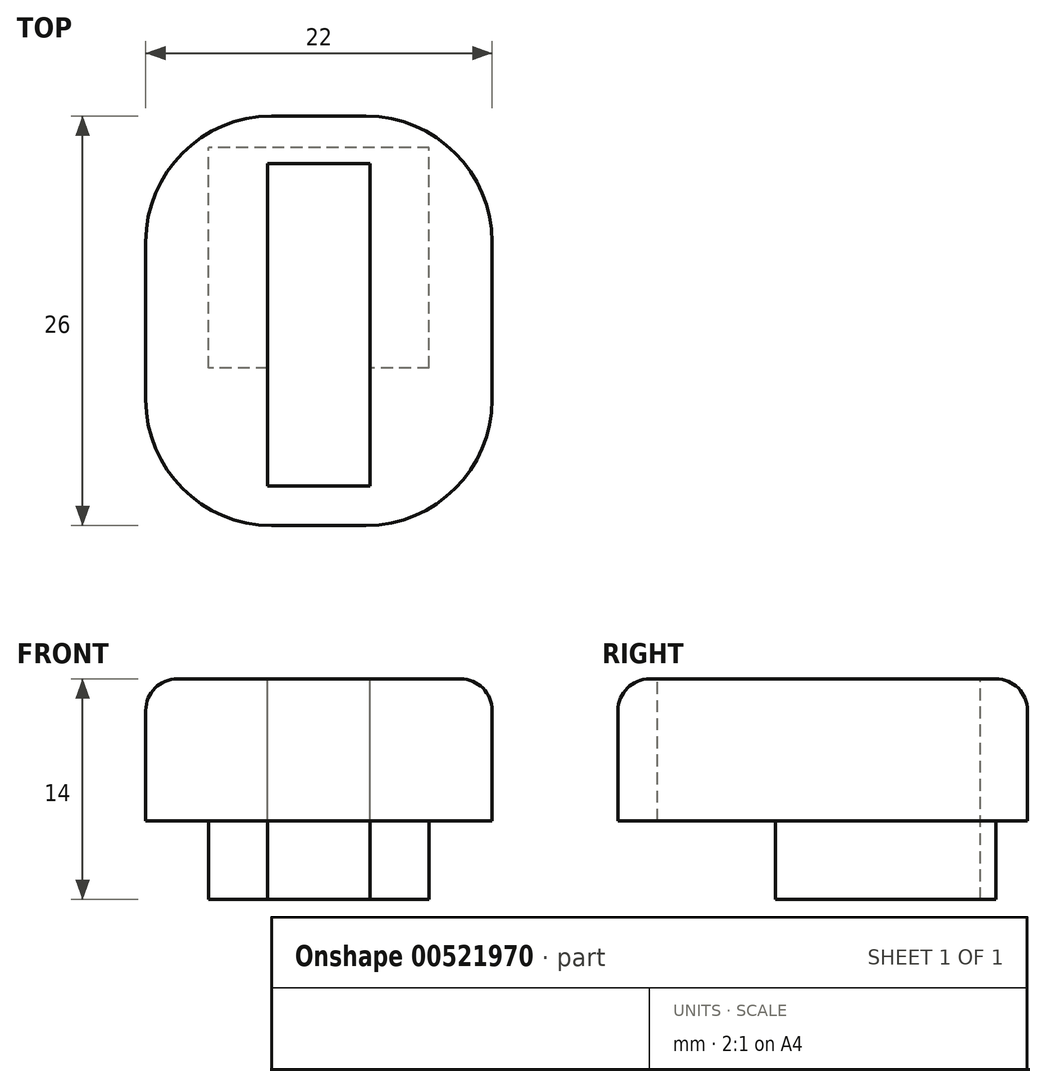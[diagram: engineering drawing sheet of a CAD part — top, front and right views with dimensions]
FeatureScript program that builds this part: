
annotation { "Feature Type Name" : "Feature", "Feature Type Description" : "" }
export const myFeature = defineFeature(function(context is Context, id is Id, definition is map)
    precondition{}
    {
        {
            var Q0;
            Q0=qCreatedBy(makeId("Top.planeOp"),FACE);
            var sketch = newSketch(context, id + "F0", { "sketchPlane" : qUnion([Q0])});
            skLineSegment(sketch, "E0.bottom", {"start": v(0, 0) * mm, "end": v(-14, 0) * mm});
            skLineSegment(sketch, "E0.top", {"start": v(0, 14) * mm, "end": v(-14, 14) * mm});
            skLineSegment(sketch, "E0.left", {"start": v(0, 0) * mm, "end": v(0, 14) * mm});
            skLineSegment(sketch, "E0.right", {"start": v(-14, 0) * mm, "end": v(-14, 14) * mm});
            skSolve(sketch);
        }
        {
            var Q0;
            Q0 = qSketchRegion(id + "F0", true);
            var Q1;
            Q1=makeQuery(id+"F0.imprint","IMPRINT",FACE,{"disambiguationData":[TD([[makeQuery(id+"F0.imprint","IMPRINT",EDGE,{"derivedFrom":sQuery(id+"F0.wireOp",EDGE,"E0.bottom")}),-1.0]])]});
            extrude(context, id + "F1", {"entities" : qUnion([Q0, Q1]), "depth" : 5 * mm, "offsetDistance" : 25 * mm});
        }
        {
            var Q0;
            Q0=makeQuery(id+"F1.opExtrude","CAP_FACE",FACE,{"disambiguationData":[OSD([sQuery(id+"F0.wireOp",EDGE,"E0.bottom"),sQuery(id+"F0.wireOp",EDGE,"E0.top"),sQuery(id+"F0.wireOp",EDGE,"E0.left"),sQuery(id+"F0.wireOp",EDGE,"E0.right")])],"isStart":false});
            var sketch = newSketch(context, id + "F2", { "sketchPlane" : qUnion([Q0])});
            skLineSegment(sketch, "E1.bottom", {"start": v(-18, 16) * mm, "end": v(4, 16) * mm});
            skLineSegment(sketch, "E1.top", {"start": v(-18, -10) * mm, "end": v(4, -10) * mm});
            skLineSegment(sketch, "E1.left", {"start": v(-18, 16) * mm, "end": v(-18, -10) * mm});
            skLineSegment(sketch, "E1.right", {"start": v(4, 16) * mm, "end": v(4, -10) * mm});
            skSolve(sketch);
        }
        {
            var Q0;
            Q0=makeQuery(id+"F2.imprint","IMPRINT",FACE,{"disambiguationData":[TD([[makeQuery(id+"F2.imprint","IMPRINT",EDGE,{"derivedFrom":sQuery(id+"F2.wireOp",EDGE,"E1.bottom")}),-1.0]])]});
            var Q1;
            Q1=makeQuery(id+"F2.imprint","IMPRINT",FACE,{"disambiguationData":[TD([[makeQuery(id+"F2.imprint","IMPRINT",EDGE,{"derivedFrom":makeQuery(id+"F1.opExtrude","CAP_EDGE",EDGE,{"disambiguationData":[OSD([sQuery(id+"F0.wireOp",EDGE,"E0.bottom")])],"isStart":false})}),-1.0]])]});
            extrude(context, id + "F3", {"entities" : qUnion([Q0, Q1]), "operationType" : NewBodyOperationType.ADD, "depth" : 9 * mm, "offsetDistance" : 25 * mm});
        }
        {
            var Q0;
            Q0=makeQuery(id+"F3.opExtrude","CAP_FACE",FACE,{"disambiguationData":[OSD([sQuery(id+"F2.wireOp",EDGE,"E1.bottom"),sQuery(id+"F2.wireOp",EDGE,"E1.top"),sQuery(id+"F2.wireOp",EDGE,"E1.left"),sQuery(id+"F2.wireOp",EDGE,"E1.right")])],"isStart":false});
            var sketch = newSketch(context, id + "F4", { "sketchPlane" : qUnion([Q0])});
            skLineSegment(sketch, "E2.bottom", {"start": v(-10.25, 13) * mm, "end": v(-3.75, 13) * mm});
            skLineSegment(sketch, "E2.top", {"start": v(-10.25, -7.5) * mm, "end": v(-3.75, -7.5) * mm});
            skLineSegment(sketch, "E2.left", {"start": v(-10.25, 13) * mm, "end": v(-10.25, -7.5) * mm});
            skLineSegment(sketch, "E2.right", {"start": v(-3.75, 13) * mm, "end": v(-3.75, -7.5) * mm});
            skLineSegment(sketch, "E3", {"start": v(-7, 13) * mm, "end": v(-7, 16) * mm, "construction": true});
            skSolve(sketch);
        }
        {
            var Q0;
            Q0=makeQuery(id+"F4.imprint","IMPRINT",FACE,{"disambiguationData":[TD([[makeQuery(id+"F4.imprint","IMPRINT",EDGE,{"derivedFrom":sQuery(id+"F4.wireOp",EDGE,"E2.bottom")}),-1.0]])]});
            var Q1;
            Q1=makeQuery(id+"F3.opExtrude","CAP_FACE",FACE,{"disambiguationData":[OSD([sQuery(id+"F2.wireOp",EDGE,"E1.bottom"),sQuery(id+"F2.wireOp",EDGE,"E1.top"),sQuery(id+"F2.wireOp",EDGE,"E1.left"),sQuery(id+"F2.wireOp",EDGE,"E1.right")])],"isStart":true});
            extrude(context, id + "F5", {"entities" : qUnion([Q0]), "operationType" : NewBodyOperationType.REMOVE, "endBound" : BoundingType.UP_TO_SURFACE, "oppositeDirection" : true, "depth" : 25 * mm, "endBoundEntityFace" : qUnion([Q1]), "offsetDistance" : 25 * mm});
        }
        {
            var Q0;
            Q0=makeQuery(id+"F5.boolean.opBoolean","COPY",FACE,{"derivedFrom":makeQuery(id+"F5.opExtrude","CAP_FACE",FACE,{"disambiguationData":[OSD([sQuery(id+"F4.wireOp",EDGE,"E2.bottom"),sQuery(id+"F4.wireOp",EDGE,"E2.top"),sQuery(id+"F4.wireOp",EDGE,"E2.left"),sQuery(id+"F4.wireOp",EDGE,"E2.right")])],"isStart":false})});
            var sketch = newSketch(context, id + "F6", { "sketchPlane" : qUnion([Q0])});
            skLineSegment(sketch, "E4.bottom", {"start": v(-3.75, 13) * mm, "end": v(-10.25, 13) * mm});
            skLineSegment(sketch, "E4.top", {"start": v(-3.75, 0) * mm, "end": v(-10.25, 0) * mm});
            skLineSegment(sketch, "E4.left", {"start": v(-3.75, 13) * mm, "end": v(-3.75, 0) * mm});
            skLineSegment(sketch, "E4.right", {"start": v(-10.25, 13) * mm, "end": v(-10.25, 0) * mm});
            skSolve(sketch);
        }
        {
            var Q0;
            Q0=makeQuery(id+"F6.imprint","IMPRINT",FACE,{"disambiguationData":[TD([[makeQuery(id+"F6.imprint","IMPRINT",EDGE,{"derivedFrom":sQuery(id+"F6.wireOp",EDGE,"E4.bottom")}),1.0]])]});
            extrude(context, id + "F7", {"entities" : qUnion([Q0]), "operationType" : NewBodyOperationType.REMOVE, "endBound" : BoundingType.THROUGH_ALL, "oppositeDirection" : true, "depth" : 25 * mm, "offsetDistance" : 25 * mm});
        }
        {
            var Q0;
            Q0=makeQuery(id+"F3.opExtrude","SWEPT_EDGE",EDGE,{"disambiguationData":[OSD([sQuery(id+"F2.wireOp",EDGE,"E1.top"),sQuery(id+"F2.wireOp",EDGE,"E1.right")])]});
            var Q1;
            Q1=makeQuery(id+"F3.opExtrude","SWEPT_EDGE",EDGE,{"disambiguationData":[OSD([sQuery(id+"F2.wireOp",EDGE,"E1.bottom"),sQuery(id+"F2.wireOp",EDGE,"E1.right")])]});
            var Q2;
            Q2=makeQuery(id+"F3.opExtrude","SWEPT_EDGE",EDGE,{"disambiguationData":[OSD([sQuery(id+"F2.wireOp",EDGE,"E1.bottom"),sQuery(id+"F2.wireOp",EDGE,"E1.left")])]});
            var Q3;
            Q3=makeQuery(id+"F3.opExtrude","SWEPT_EDGE",EDGE,{"disambiguationData":[OSD([sQuery(id+"F2.wireOp",EDGE,"E1.top"),sQuery(id+"F2.wireOp",EDGE,"E1.left")])]});
            fillet(context, id + "F8", {"entities" : qUnion([Q0, Q1, Q2, Q3]), "radius" : 8 * mm, "tangentPropagation" : true, "allowEdgeOverflow" : false});
        }
        {
            var Q0;
            Q0=makeQuery(id+"F3.opExtrude","CAP_EDGE",EDGE,{"disambiguationData":[OSD([sQuery(id+"F2.wireOp",EDGE,"E1.right")])],"isStart":false});
            var Q1;
            {var subQ0=sQuery(id+"F2.wireOp",EDGE,"E1.right");var subQ1=sQuery(id+"F2.wireOp",EDGE,"E1.bottom");Q1=makeQuery(id+"F8.opFillet","BLEND_EDGE",EDGE,{"blendedFrom":[makeQuery(id+"F3.opExtrude","SWEPT_EDGE",EDGE,{"disambiguationData":[OSD([subQ1,subQ0])]}),makeQuery(id+"F3.opExtrude","CAP_FACE",FACE,{"disambiguationData":[OSD([subQ1,sQuery(id+"F2.wireOp",EDGE,"E1.top"),sQuery(id+"F2.wireOp",EDGE,"E1.left"),subQ0])],"isStart":false})],"blendedInto":[makeQuery(id+"F3.opExtrude","CAP_FACE",FACE,{"disambiguationData":[OSD([subQ1,sQuery(id+"F2.wireOp",EDGE,"E1.top"),sQuery(id+"F2.wireOp",EDGE,"E1.left"),subQ0])],"isStart":false})]});}
            fillet(context, id + "F9", {"entities" : qUnion([Q0, Q1]), "radius" : 2 * mm, "tangentPropagation" : true, "allowEdgeOverflow" : false});
        }
    });
